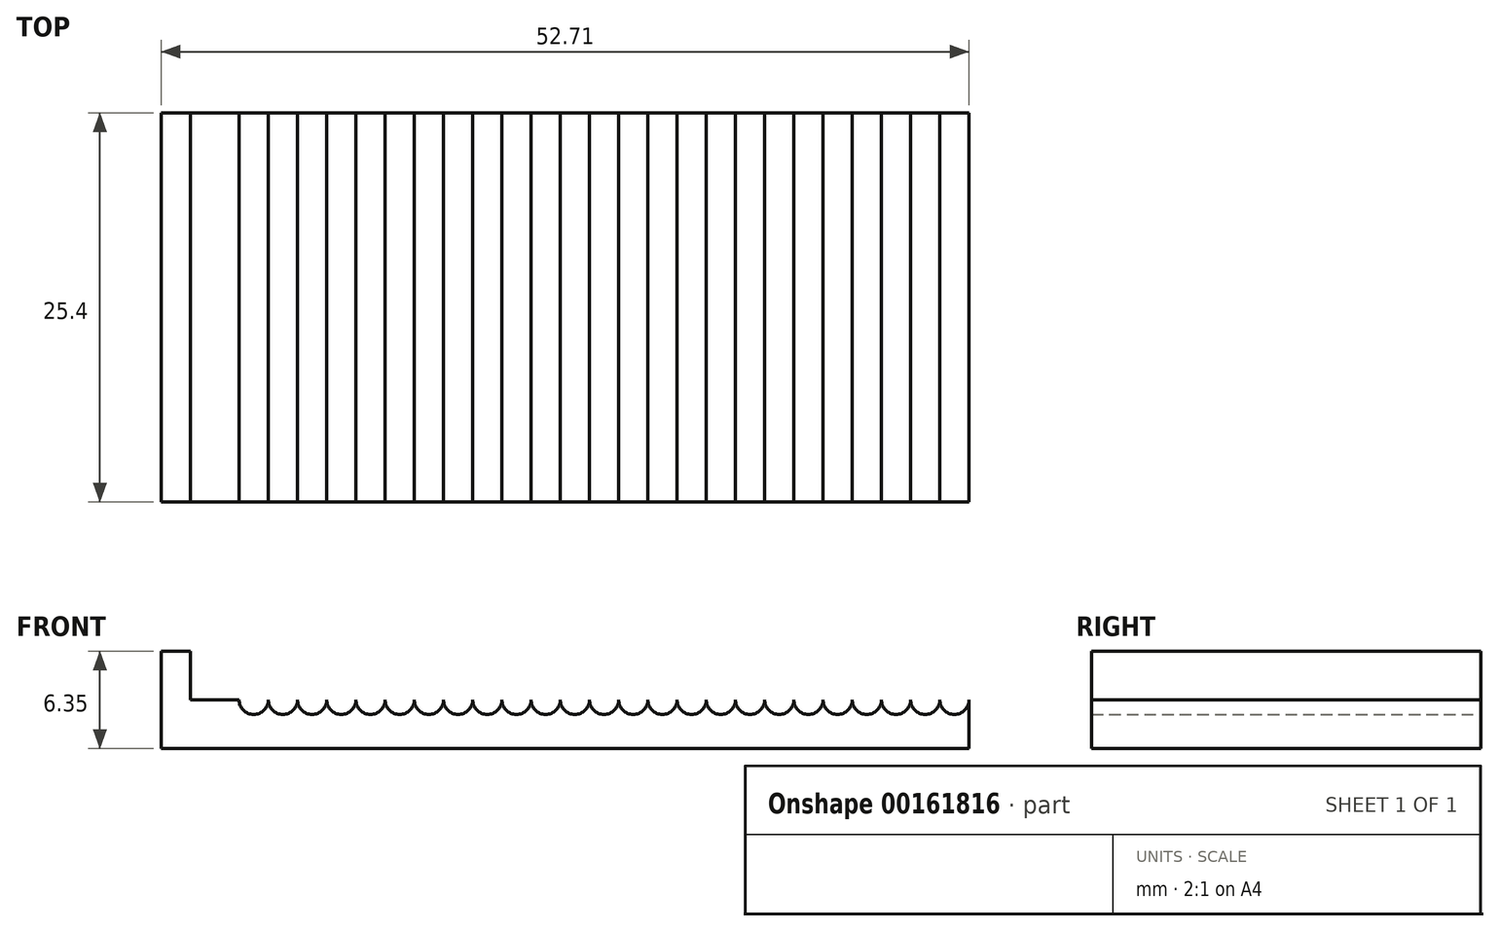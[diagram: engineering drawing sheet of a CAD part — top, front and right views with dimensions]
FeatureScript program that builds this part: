
annotation { "Feature Type Name" : "Feature", "Feature Type Description" : "" }
export const myFeature = defineFeature(function(context is Context, id is Id, definition is map)
    precondition{}
    {
        {
            var Q0;
            Q0=qCreatedBy(makeId("Front.planeOp"), FACE);
            var sketch = newSketch(context, id + "F0", { "sketchPlane" : qUnion([Q0])});
            skLineSegment(sketch, "E0", {"start": v(0, 0) * mm, "end": v(50.8, 0) * mm});
            skLineSegment(sketch, "E1", {"start": v(50.8, 0) * mm, "end": v(50.8, 3.17) * mm});
            skLineSegment(sketch, "E2.bottom", {"start": v(0, 0) * mm, "end": v(-1.9, 0) * mm});
            skLineSegment(sketch, "E2.top", {"start": v(0, 6.35) * mm, "end": v(-1.9, 6.35) * mm});
            skLineSegment(sketch, "E2.left", {"start": v(0, 3.17) * mm, "end": v(0, 6.35) * mm});
            skLineSegment(sketch, "E2.right", {"start": v(-1.9, 0) * mm, "end": v(-1.9, 6.35) * mm});
            skArc(sketch, "E3", {"start": v(48.9, 3.17) * mm, "mid": v(49.85, 2.22) * mm, "end": v(50.8, 3.17) * mm});
            skArc(sketch, "E4.1.0.0", {"start": v(47, 3.17) * mm, "mid": v(47.94, 2.22) * mm, "end": v(48.9, 3.17) * mm});
            skArc(sketch, "E4.2.0.0", {"start": v(45.09, 3.17) * mm, "mid": v(46.04, 2.22) * mm, "end": v(47, 3.17) * mm});
            skArc(sketch, "E4.3.0.0", {"start": v(43.18, 3.17) * mm, "mid": v(44.13, 2.22) * mm, "end": v(45.09, 3.17) * mm});
            skArc(sketch, "E4.4.0.0", {"start": v(41.28, 3.17) * mm, "mid": v(42.23, 2.22) * mm, "end": v(43.18, 3.17) * mm});
            skArc(sketch, "E4.5.0.0", {"start": v(39.37, 3.17) * mm, "mid": v(40.32, 2.22) * mm, "end": v(41.28, 3.17) * mm});
            skArc(sketch, "E4.6.0.0", {"start": v(37.47, 3.17) * mm, "mid": v(38.42, 2.22) * mm, "end": v(39.37, 3.17) * mm});
            skArc(sketch, "E4.7.0.0", {"start": v(35.56, 3.17) * mm, "mid": v(36.51, 2.22) * mm, "end": v(37.47, 3.17) * mm});
            skArc(sketch, "E4.8.0.0", {"start": v(33.66, 3.17) * mm, "mid": v(34.6, 2.22) * mm, "end": v(35.56, 3.17) * mm});
            skArc(sketch, "E4.9.0.0", {"start": v(31.75, 3.17) * mm, "mid": v(32.7, 2.22) * mm, "end": v(33.66, 3.17) * mm});
            skArc(sketch, "E4.10.0.0", {"start": v(29.85, 3.17) * mm, "mid": v(30.8, 2.22) * mm, "end": v(31.75, 3.17) * mm});
            skArc(sketch, "E4.11.0.0", {"start": v(27.94, 3.17) * mm, "mid": v(28.9, 2.22) * mm, "end": v(29.85, 3.17) * mm});
            skArc(sketch, "E4.12.0.0", {"start": v(26.04, 3.17) * mm, "mid": v(26.99, 2.22) * mm, "end": v(27.94, 3.17) * mm});
            skArc(sketch, "E4.13.0.0", {"start": v(24.13, 3.17) * mm, "mid": v(25.08, 2.22) * mm, "end": v(26.04, 3.17) * mm});
            skArc(sketch, "E4.14.0.0", {"start": v(22.23, 3.17) * mm, "mid": v(23.18, 2.22) * mm, "end": v(24.13, 3.17) * mm});
            skArc(sketch, "E4.15.0.0", {"start": v(20.32, 3.17) * mm, "mid": v(21.27, 2.22) * mm, "end": v(22.23, 3.17) * mm});
            skArc(sketch, "E4.16.0.0", {"start": v(18.42, 3.17) * mm, "mid": v(19.37, 2.22) * mm, "end": v(20.32, 3.17) * mm});
            skArc(sketch, "E4.17.0.0", {"start": v(16.51, 3.17) * mm, "mid": v(17.46, 2.22) * mm, "end": v(18.42, 3.17) * mm});
            skArc(sketch, "E4.18.0.0", {"start": v(14.6, 3.17) * mm, "mid": v(15.56, 2.22) * mm, "end": v(16.51, 3.17) * mm});
            skArc(sketch, "E4.19.0.0", {"start": v(12.7, 3.17) * mm, "mid": v(13.65, 2.22) * mm, "end": v(14.6, 3.17) * mm});
            skArc(sketch, "E4.20.0.0", {"start": v(10.8, 3.17) * mm, "mid": v(11.75, 2.22) * mm, "end": v(12.7, 3.17) * mm});
            skArc(sketch, "E4.21.0.0", {"start": v(8.9, 3.17) * mm, "mid": v(9.84, 2.22) * mm, "end": v(10.8, 3.17) * mm});
            skArc(sketch, "E4.22.0.0", {"start": v(6.99, 3.17) * mm, "mid": v(7.94, 2.22) * mm, "end": v(8.9, 3.17) * mm});
            skArc(sketch, "E4.23.0.0", {"start": v(5.08, 3.17) * mm, "mid": v(6.03, 2.22) * mm, "end": v(6.99, 3.17) * mm});
            skArc(sketch, "E4.24.0.0", {"start": v(3.18, 3.17) * mm, "mid": v(4.13, 2.22) * mm, "end": v(5.08, 3.17) * mm});
            skLineSegment(sketch, "E4.direction1", {"start": v(48.9, 3.17) * mm, "end": v(47, 3.17) * mm, "construction": true});
            skLineSegment(sketch, "E5", {"start": v(3.18, 3.17) * mm, "end": v(0, 3.17) * mm});
            skSolve(sketch);
        }
        {
            var Q0;
            Q0 = qSketchRegion(id + "F0", true);
            extrude(context, id + "F1", {"entities" : qUnion([Q0]), "depth" : 25.4 * mm, "offsetDistance" : 25.4 * mm});
        }
    });
